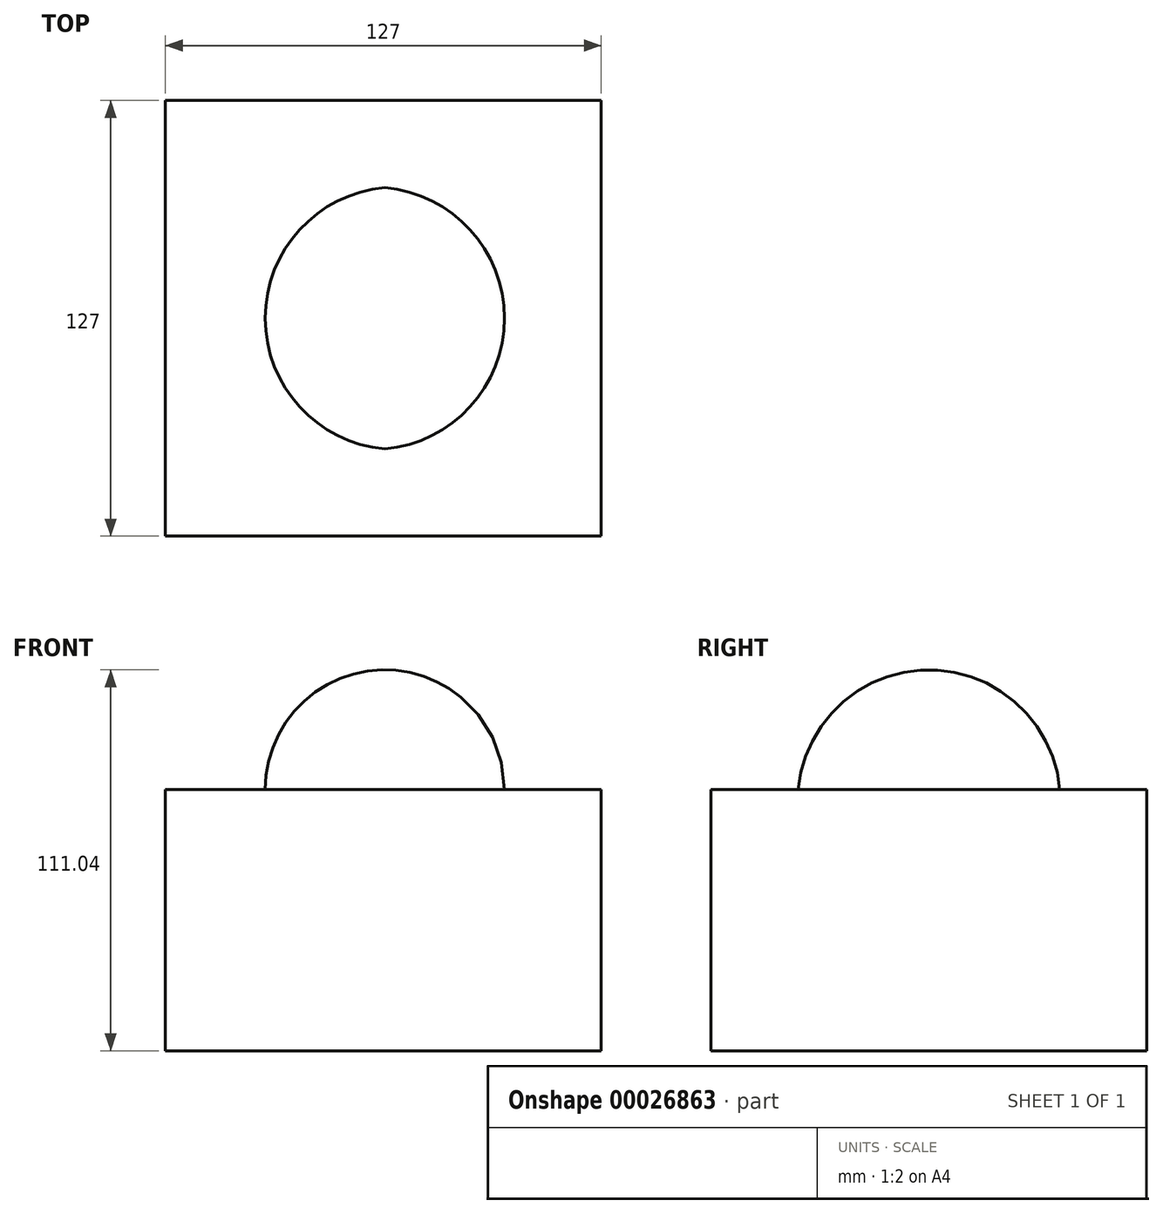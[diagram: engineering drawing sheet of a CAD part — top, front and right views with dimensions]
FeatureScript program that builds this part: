
annotation { "Feature Type Name" : "Feature", "Feature Type Description" : "" }
export const myFeature = defineFeature(function(context is Context, id is Id, definition is map)
    precondition{}
    {
        {
            var Q0;
            Q0=qCreatedBy(makeId("Top.planeOp"),FACE);
            var sketch = newSketch(context, id + "F0", { "sketchPlane" : qUnion([Q0])});
            skLineSegment(sketch, "E0.bottom", {"start": v(-63.91, 69.52) * mm, "end": v(63.09, 69.52) * mm});
            skLineSegment(sketch, "E0.top", {"start": v(-63.91, -57.48) * mm, "end": v(63.09, -57.48) * mm});
            skLineSegment(sketch, "E0.left", {"start": v(-63.91, 69.52) * mm, "end": v(-63.91, -57.48) * mm});
            skLineSegment(sketch, "E0.right", {"start": v(63.09, 69.52) * mm, "end": v(63.09, -57.48) * mm});
            skSolve(sketch);
        }
        {
            var Q0;
            Q0=makeQuery(id+"F0.imprint","IMPRINT",FACE,{"disambiguationData":[TD([[makeQuery(id+"F0.imprint","IMPRINT",EDGE,{"derivedFrom":sQuery(id+"F0.wireOp",EDGE,"E0.bottom")}),-1.0]])]});
            extrude(context, id + "F1", {"entities" : qUnion([Q0]), "depth" : 76.2 * mm});
        }
        {
            var Q0;
            Q0=makeQuery(id+"F1.opExtrude","CAP_FACE",FACE,{"disambiguationData":[OSD([sQuery(id+"F0.wireOp",EDGE,"E0.bottom"),sQuery(id+"F0.wireOp",EDGE,"E0.top"),sQuery(id+"F0.wireOp",EDGE,"E0.left"),sQuery(id+"F0.wireOp",EDGE,"E0.right")])],"isStart":false});
            var sketch = newSketch(context, id + "F2", { "sketchPlane" : qUnion([Q0])});
            skArc(sketch, "E1", {"start": v(0, -32.08) * mm, "mid": v(34.84, 6.02) * mm, "end": v(0, 44.12) * mm});
            skLineSegment(sketch, "E2", {"start": v(0, 44.12) * mm, "end": v(0, -32.08) * mm});
            skSolve(sketch);
        }
        {
            var Q0;
            Q0=makeQuery(id+"F2.imprint","IMPRINT",FACE,{"disambiguationData":[TD([[makeQuery(id+"F2.imprint","IMPRINT",EDGE,{"derivedFrom":sQuery(id+"F2.wireOp",EDGE,"E1")}),1.0]])]});
            var Q1;
            Q1=sQuery(id+"F2.wireOp",EDGE,"E2");
            revolve(context, id + "F3", {"operationType" : NewBodyOperationType.ADD, "entities" : qUnion([Q0]), "axis" : qUnion([Q1]), "revolveType" : RevolveType.FULL, "oppositeDirection" : true});
        }
    });
